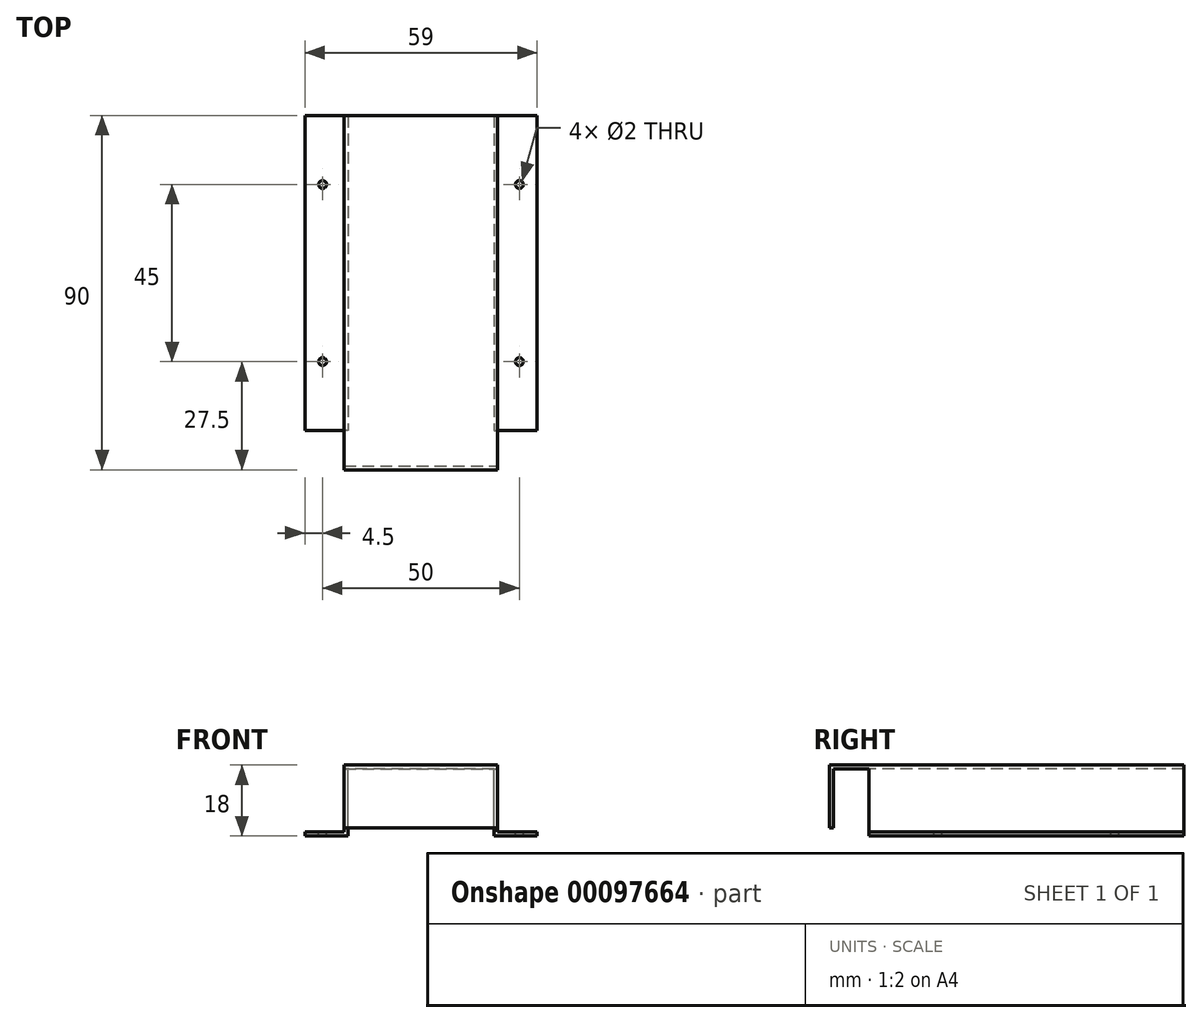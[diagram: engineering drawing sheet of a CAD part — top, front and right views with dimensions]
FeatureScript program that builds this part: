
annotation { "Feature Type Name" : "Feature", "Feature Type Description" : "" }
export const myFeature = defineFeature(function(context is Context, id is Id, definition is map)
    precondition{}
    {
        {
            var Q0;
            Q0=qCreatedBy(makeId("Top.planeOp"),FACE);
            var sketch = newSketch(context, id + "F0", { "sketchPlane" : qUnion([Q0])});
            skLineSegment(sketch, "E0.bottom", {"start": v(19.5, 45) * mm, "end": v(-19.5, 45) * mm});
            skLineSegment(sketch, "E0.top", {"start": v(19.5, -45) * mm, "end": v(-19.5, -45) * mm});
            skLineSegment(sketch, "E0.left", {"start": v(19.5, 45) * mm, "end": v(19.5, -45) * mm});
            skLineSegment(sketch, "E0.right", {"start": v(-19.5, 45) * mm, "end": v(-19.5, -45) * mm});
            skPoint(sketch, "E0.middle", {"position": v(0, 0) * mm});
            skSolve(sketch);
        }
        {
            var Q0;
            Q0 = qSketchRegion(id + "F0", true);
            extrude(context, id + "F1", {"entities" : qUnion([Q0]), "depth" : 1 * mm});
        }
        {
            var Q0;
            Q0=makeQuery(id+"F1.opExtrude","CAP_FACE",FACE,{"disambiguationData":[OSD([sQuery(id+"F0.wireOp",EDGE,"E0.bottom"),sQuery(id+"F0.wireOp",EDGE,"E0.top"),sQuery(id+"F0.wireOp",EDGE,"E0.left"),sQuery(id+"F0.wireOp",EDGE,"E0.right")])],"isStart":true});
            var sketch = newSketch(context, id + "F2", { "sketchPlane" : qUnion([Q0])});
            skLineSegment(sketch, "E1.bottom", {"start": v(19.5, -45) * mm, "end": v(18.5, -45) * mm});
            skLineSegment(sketch, "E1.top", {"start": v(19.5, 45) * mm, "end": v(18.5, 45) * mm});
            skLineSegment(sketch, "E1.left", {"start": v(19.5, -45) * mm, "end": v(19.5, 45) * mm});
            skLineSegment(sketch, "E1.right", {"start": v(18.5, -45) * mm, "end": v(18.5, 45) * mm});
            skSolve(sketch);
        }
        {
            var Q0;
            Q0 = qSketchRegion(id + "F2", true);
            extrude(context, id + "F3", {"entities" : qUnion([Q0]), "operationType" : NewBodyOperationType.ADD, "depth" : 17 * mm});
        }
        {
            var Q0;
            Q0=makeQuery(id+"F3.boolean.opBoolean","MERGE",FACE,{"derivedFrom":[makeQuery(id+"F1.opExtrude","SWEPT_FACE",FACE,{"disambiguationData":[OSD([sQuery(id+"F0.wireOp",EDGE,"E0.left")])]}),makeQuery(id+"F3.opExtrude","SWEPT_FACE",FACE,{"disambiguationData":[OSD([sQuery(id+"F2.wireOp",EDGE,"E1.left")])]})]});
            var sketch = newSketch(context, id + "F4", { "sketchPlane" : qUnion([Q0])});
            skLineSegment(sketch, "E2.bottom", {"start": v(-45, -17) * mm, "end": v(45, -17) * mm});
            skLineSegment(sketch, "E2.top", {"start": v(-45, -16) * mm, "end": v(45, -16) * mm});
            skLineSegment(sketch, "E2.left", {"start": v(-45, -17) * mm, "end": v(-45, -16) * mm});
            skLineSegment(sketch, "E2.right", {"start": v(45, -17) * mm, "end": v(45, -16) * mm});
            skSolve(sketch);
        }
        {
            var Q0;
            Q0 = qSketchRegion(id + "F4", true);
            extrude(context, id + "F5", {"entities" : qUnion([Q0]), "operationType" : NewBodyOperationType.ADD, "depth" : 10 * mm});
        }
        {
            var Q0;
            Q0=makeQuery(id+"F5.opExtrude","CAP_FACE",FACE,{"disambiguationData":[OSD([sQuery(id+"F4.wireOp",EDGE,"E2.bottom"),sQuery(id+"F4.wireOp",EDGE,"E2.top"),sQuery(id+"F4.wireOp",EDGE,"E2.left"),sQuery(id+"F4.wireOp",EDGE,"E2.right")])],"isStart":false});
            var sketch = newSketch(context, id + "F6", { "sketchPlane" : qUnion([Q0])});
            skLineSegment(sketch, "E3.bottom", {"start": v(-45, -17) * mm, "end": v(-35, -17) * mm});
            skLineSegment(sketch, "E3.top", {"start": v(-45, 1) * mm, "end": v(-35, 1) * mm});
            skLineSegment(sketch, "E3.left", {"start": v(-45, -17) * mm, "end": v(-45, 1) * mm});
            skLineSegment(sketch, "E3.right", {"start": v(-35, -17) * mm, "end": v(-35, 1) * mm});
            skLineSegment(sketch, "E4.0", {"start": v(-35, 1) * mm, "end": v(-45, 1) * mm});
            skPoint(sketch, "E5.orphan", {"position": v(45, 1) * mm});
            skSolve(sketch);
        }
        {
            var Q0;
            Q0 = qSketchRegion(id + "F6", true);
            var Q1;
            Q1=makeQuery(id+"F3.opExtrude","SWEPT_FACE",FACE,{"disambiguationData":[OSD([sQuery(id+"F2.wireOp",EDGE,"E1.right")])]});
            extrude(context, id + "F7", {"entities" : qUnion([Q0]), "operationType" : NewBodyOperationType.REMOVE, "endBound" : BoundingType.UP_TO_SURFACE, "oppositeDirection" : true, "endBoundEntityFace" : qUnion([Q1]), "depth" : 25 * mm});
        }
        {
            var Q0;
            Q0=makeQuery(id+"F1.opExtrude","CAP_FACE",FACE,{"disambiguationData":[OSD([sQuery(id+"F0.wireOp",EDGE,"E0.bottom"),sQuery(id+"F0.wireOp",EDGE,"E0.top"),sQuery(id+"F0.wireOp",EDGE,"E0.left"),sQuery(id+"F0.wireOp",EDGE,"E0.right")])],"isStart":true});
            var sketch = newSketch(context, id + "F8", { "sketchPlane" : qUnion([Q0])});
            skLineSegment(sketch, "E6.bottom", {"start": v(-19.5, 45) * mm, "end": v(18.5, 45) * mm});
            skLineSegment(sketch, "E6.top", {"start": v(-19.5, 44) * mm, "end": v(18.5, 44) * mm});
            skLineSegment(sketch, "E6.left", {"start": v(-19.5, 45) * mm, "end": v(-19.5, 44) * mm});
            skLineSegment(sketch, "E6.right", {"start": v(18.5, 45) * mm, "end": v(18.5, 44) * mm});
            skSolve(sketch);
        }
        {
            var Q0;
            Q0 = qSketchRegion(id + "F8", true);
            extrude(context, id + "F9", {"entities" : qUnion([Q0]), "operationType" : NewBodyOperationType.ADD, "depth" : 15 * mm});
        }
        {
            var Q0;
            Q0=makeQuery(id+"F5.opExtrude","SWEPT_FACE",FACE,{"disambiguationData":[OSD([sQuery(id+"F4.wireOp",EDGE,"E2.top")])]});
            var sketch = newSketch(context, id + "F10", { "sketchPlane" : qUnion([Q0])});
            skLineSegment(sketch, "E7", {"start": v(29.5, 5) * mm, "end": v(19.5, 5) * mm, "construction": true});
            skCircle(sketch, "E8", {"center": v(25, 27.5) * mm, "radius": 1 * mm});
            skCircle(sketch, "E9.MirrorC", {"center": v(25, -17.5) * mm, "radius": 1 * mm});
            skSolve(sketch);
        }
        {
            var Q0;
            Q0 = qSketchRegion(id + "F10", true);
            extrude(context, id + "F11", {"entities" : qUnion([Q0]), "operationType" : NewBodyOperationType.REMOVE, "endBound" : BoundingType.UP_TO_NEXT, "oppositeDirection" : true, "depth" : 25 * mm});
        }
        {
            var Q0;
            Q0=makeQuery(id+"F1.opExtrude","SWEPT_BODY",BODY,{"disambiguationData":[OSD([sQuery(id+"F0.wireOp",EDGE,"E0.bottom"),sQuery(id+"F0.wireOp",EDGE,"E0.top"),sQuery(id+"F0.wireOp",EDGE,"E0.left"),sQuery(id+"F0.wireOp",EDGE,"E0.right")])]});
            var Q1;
            Q1=qCreatedBy(makeId("Right.planeOp"),FACE);
            mirror(context, id + "F12", {"operationType" : NewBodyOperationType.ADD, "entities" : qUnion([Q0]), "mirrorPlane" : qUnion([Q1])});
        }
    });
